# Revit family: Haworth_Planes_ColumnBaseConferenceTable_DTop
name_source: partatom
category: Furniture Systems
revit_build: Autodesk Revit 2018 (Build: 20170223_1515(x64)
units: mm (PartAtom-declared; Revit-internal decimal feet)

## family parameters
Always vertical = Yes
Cut with Voids When Loaded = No
OmniClass Number = 23.40.70.14.64.21
OmniClass Title = Systems Furniture
Part Type = Normal
Room Calculation Point = No
Round Connector Dimension = Use Diameter
Shared = No
Work Plane-Based = No

## types (14) — shared parameters
42 Depth Limits = Available Widths = 48, 54, 60, 66, 72
48 Depth Limits = Available Widths = 48, 54, 60, 66, 72
54 Depth Limits = Available Widths = 54, 60, 66, 72
60 Depth Limits = Available Widths = 60, 66, 72, 78, 84
Actual Height = 29"
Assembly Code = E2020200
Base Finish = Haworth _ Paint _ Black
Base Plate Round = No
Base Plate Square = Yes
Cladding Round = No
Cladding Square = Yes
Description = Haworth - Planes - Column Base Conferencce Table - D Top
Height = 29"
Manufacturer = Haworth
Max. Depth = 60"
Max. Height = 42"
Min. Depth = 42"
Min. Height = 29"
Model = Haworth - Planes - Column Base Conferencce Table - D Top
Revision Number = 2
Size = Verify Final Dim. w/ Haworth
Support Finish = Haworth _ Paint _ Black
Support Height = 27 13/16"
Support Location = 24"
Support Panel Finish = Haworth _ Laminate _ Maple H-AE
Sustainability Info = http://www.haworth.com
Table Thickness = 1 3/16"
URL = http://www.haworth.com
URL - Product = http://www.haworth.com
Warranty = http://www.haworth.com
Worksurface Edge Finish = Haworth _ Laminate _ Maple H-AE
Worksurface Finish = Haworth _ Laminate _ Maple H-AE

## per-type parameters (varying)
| type | Actual Depth | Actual Width | Depth | Half Depth | Max. Width | Min. Width | Width |
| 48w 48d | 48" | 48" | 48" | 24" | 72" | 48" | 48" |
| 54w 48d | 48" | 54" | 48" | 24" | 72" | 48" | 54" |
| 60w 48d | 48" | 60" | 48" | 24" | 72" | 48" | 60" |
| 66w 48d | 48" | 66" | 48" | 24" | 72" | 48" | 66" |
| 72w 48d | 48" | 72" | 48" | 24" | 72" | 48" | 72" |
| 48w 54d | 54" | 54" | 54" | 27" | 72" | 54" | 48" |
| 60w 54d | 54" | 60" | 54" | 27" | 72" | 54" | 60" |
| 66w 54d | 54" | 66" | 54" | 27" | 72" | 54" | 66" |
| 72w 54d | 54" | 72" | 54" | 27" | 72" | 54" | 72" |
| 60w 60d | 60" | 60" | 60" | 30" | 84" | 60" | 60" |
| 66w 60d | 60" | 66" | 60" | 30" | 84" | 60" | 66" |
| 72w 60d | 60" | 72" | 60" | 30" | 84" | 60" | 72" |
| 78w 60d | 60" | 78" | 60" | 30" | 84" | 60" | 78" |
| 84w 60d | 60" | 84" | 60" | 30" | 84" | 60" | 84" |

## geometry (parser evidence)
native form markers: Sweep x6
no freeform markers — native parametric forms only
